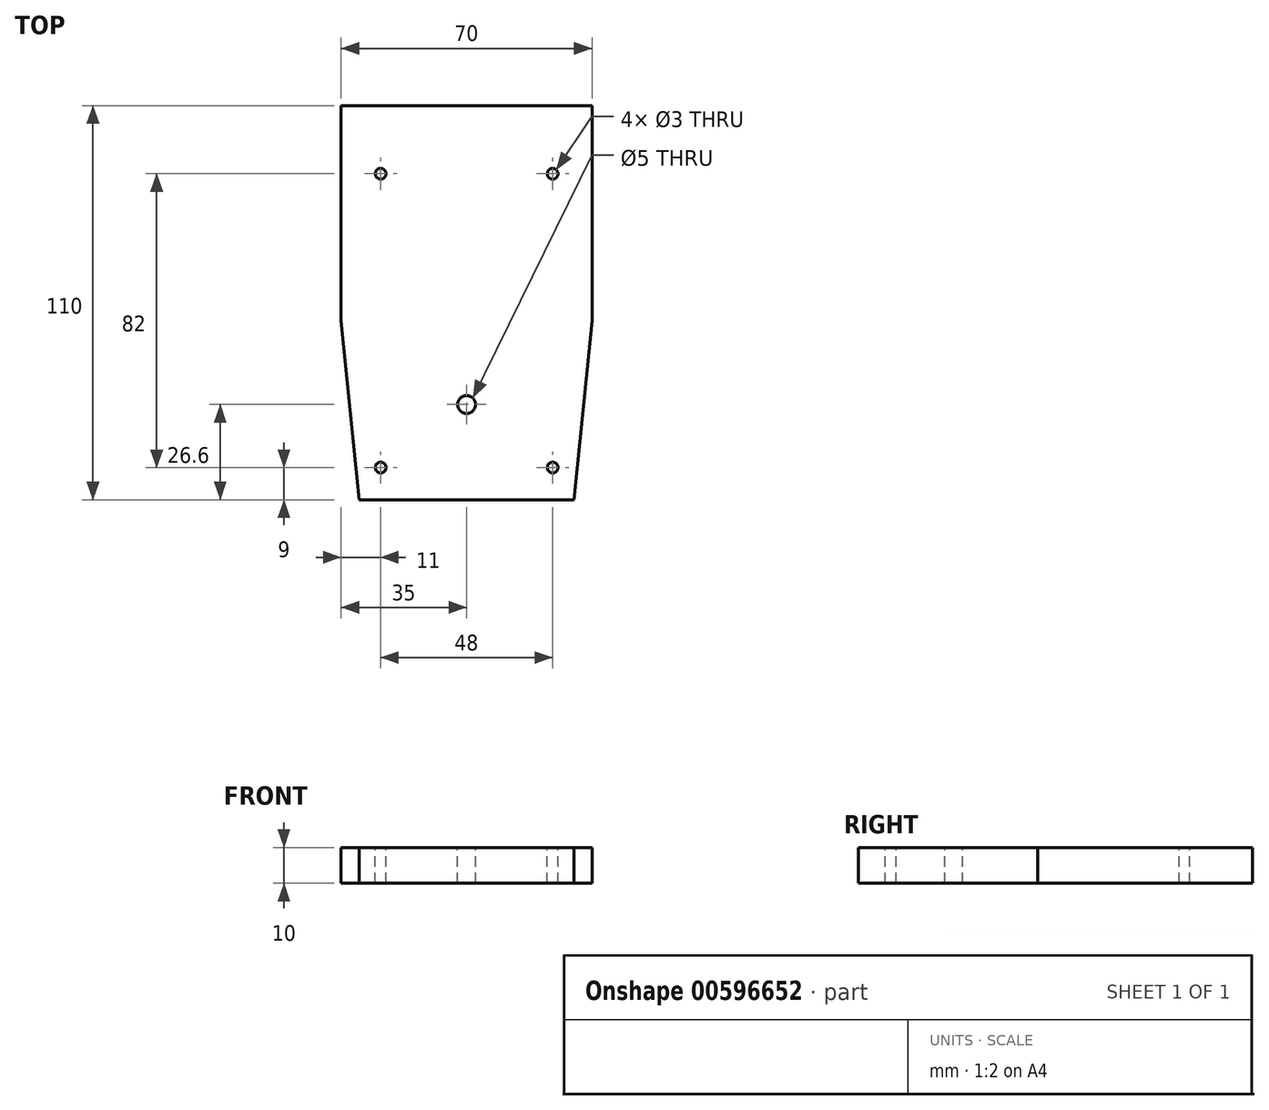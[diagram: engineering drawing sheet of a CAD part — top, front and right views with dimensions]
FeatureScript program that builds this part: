
annotation { "Feature Type Name" : "Feature", "Feature Type Description" : "" }
export const myFeature = defineFeature(function(context is Context, id is Id, definition is map)
    precondition{}
    {
        {
            var Q0;
            Q0=qCreatedBy(makeId("Top.planeOp"),FACE);
            var sketch = newSketch(context, id + "F0", { "sketchPlane" : qUnion([Q0])});
            skLineSegment(sketch, "E0.bottom", {"start": v(35, 55) * mm, "end": v(-35, 55) * mm});
            skLineSegment(sketch, "E0.top", {"start": v(30, -55) * mm, "end": v(-30, -55) * mm});
            skLineSegment(sketch, "E0.left", {"start": v(35, 55) * mm, "end": v(35, -5) * mm});
            skLineSegment(sketch, "E0.right", {"start": v(-35, 55) * mm, "end": v(-35, -5) * mm});
            skPoint(sketch, "E0.middle", {"position": v(0, 0) * mm});
            skLineSegment(sketch, "E1", {"start": v(-70.7, -5) * mm, "end": v(55.02, -5) * mm, "construction": true});
            skLineSegment(sketch, "E2", {"start": v(30, -57.27) * mm, "end": v(30, 7.3) * mm, "construction": true});
            skLineSegment(sketch, "E3", {"start": v(-30, -57.9) * mm, "end": v(-30, 7.93) * mm, "construction": true});
            skLineSegment(sketch, "E4", {"start": v(0, -71) * mm, "end": v(0, 65.02) * mm, "construction": true});
            skPoint(sketch, "E4.endSnap0", {"position": v(0, 55) * mm});
            skLineSegment(sketch, "E5", {"start": v(-30, -55) * mm, "end": v(-35, -5) * mm});
            skLineSegment(sketch, "E6", {"start": v(35, -5) * mm, "end": v(30, -55) * mm});
            skPoint(sketch, "E7.orphan", {"position": v(-35, -55) * mm});
            skPoint(sketch, "E8.orphan", {"position": v(35, -55) * mm});
            skSolve(sketch);
        }
        {
            var Q0;
            Q0=makeQuery(id+"F0.imprint","IMPRINT",FACE,{"disambiguationData":[TD([[makeQuery(id+"F0.imprint","IMPRINT",EDGE,{"derivedFrom":sQuery(id+"F0.wireOp",EDGE,"E0.bottom")}),1.0]])]});
            extrude(context, id + "F1", {"entities" : qUnion([Q0]), "depth" : 10 * mm, "offsetDistance" : 25 * mm});
        }
        {
            var Q0;
            Q0=makeQuery(id+"F1.opExtrude","CAP_FACE",FACE,{"disambiguationData":[OSD([sQuery(id+"F0.wireOp",EDGE,"E0.bottom"),sQuery(id+"F0.wireOp",EDGE,"E0.top"),sQuery(id+"F0.wireOp",EDGE,"E0.left"),sQuery(id+"F0.wireOp",EDGE,"E0.right"),sQuery(id+"F0.wireOp",EDGE,"E5"),sQuery(id+"F0.wireOp",EDGE,"E6")])],"isStart":false});
            var sketch = newSketch(context, id + "F2", { "sketchPlane" : qUnion([Q0])});
            skLineSegment(sketch, "E9", {"start": v(-80.97, 36) * mm, "end": v(80.97, 36) * mm, "construction": true});
            skLineSegment(sketch, "E10", {"start": v(-24, 60.66) * mm, "end": v(-24, -66.93) * mm, "construction": true});
            skLineSegment(sketch, "E11", {"start": v(24, 62.09) * mm, "end": v(24, -66.65) * mm, "construction": true});
            skPoint(sketch, "E12", {"position": v(24, 36) * mm});
            skPoint(sketch, "E13", {"position": v(-24, 36) * mm});
            skLineSegment(sketch, "E14", {"start": v(-79.03, -46) * mm, "end": v(83.88, -46) * mm, "construction": true});
            skPoint(sketch, "E15", {"position": v(-24, -46) * mm});
            skPoint(sketch, "E16", {"position": v(24, -46) * mm});
            skLineSegment(sketch, "E17", {"start": v(0, -61.23) * mm, "end": v(0, 63.51) * mm, "construction": true});
            skPoint(sketch, "E17.endSnap0", {"position": v(0, 55) * mm});
            skLineSegment(sketch, "E18", {"start": v(-54.9, -28.4) * mm, "end": v(59.3, -28.4) * mm, "construction": true});
            skLineSegment(sketch, "E19", {"start": v(69.27, 55) * mm, "end": v(-59.18, 55) * mm, "construction": true});
            skPoint(sketch, "E20", {"position": v(0, -28.4) * mm});
            skSolve(sketch);
        }
        {
            var Q0;
            Q0=sQuery(id+"F2.wireOp",VERTEX,"E20");
            var Q1;
            Q1=makeQuery(id+"F1.opExtrude","SWEPT_BODY",BODY,{"disambiguationData":[OSD([sQuery(id+"F0.wireOp",EDGE,"E0.bottom"),sQuery(id+"F0.wireOp",EDGE,"E0.top"),sQuery(id+"F0.wireOp",EDGE,"E0.left"),sQuery(id+"F0.wireOp",EDGE,"E0.right"),sQuery(id+"F0.wireOp",EDGE,"E5"),sQuery(id+"F0.wireOp",EDGE,"E6")])]});
            hole(context, id + "F3", {"style" : HoleStyle.SIMPLE, "endStyle" : HoleEndStyle.THROUGH, "holeDiameter" : 5 * mm, "majorDiameter" : 5 * mm, "isTappedThrough" : true, "tappedDepth" : 12 * mm, "tapClearance" : 3, "locations" : qUnion([Q0]), "scope" : qUnion([Q1])});
        }
        {
            var Q0;
            Q0=sQuery(id+"F2.wireOp",VERTEX,"E13");
            var Q1;
            Q1=sQuery(id+"F2.wireOp",VERTEX,"E12");
            var Q2;
            Q2=sQuery(id+"F2.wireOp",VERTEX,"E16");
            var Q3;
            Q3=sQuery(id+"F2.wireOp",VERTEX,"E15");
            var Q4;
            Q4=makeQuery(id+"F1.opExtrude","SWEPT_BODY",BODY,{"disambiguationData":[OSD([sQuery(id+"F0.wireOp",EDGE,"E0.bottom"),sQuery(id+"F0.wireOp",EDGE,"E0.top"),sQuery(id+"F0.wireOp",EDGE,"E0.left"),sQuery(id+"F0.wireOp",EDGE,"E0.right"),sQuery(id+"F0.wireOp",EDGE,"E5"),sQuery(id+"F0.wireOp",EDGE,"E6")])]});
            hole(context, id + "F4", {"style" : HoleStyle.SIMPLE, "endStyle" : HoleEndStyle.THROUGH, "holeDiameter" : 3 * mm, "majorDiameter" : 5 * mm, "isTappedThrough" : true, "tappedDepth" : 12 * mm, "tapClearance" : 3, "locations" : qUnion([Q0, Q1, Q2, Q3]), "scope" : qUnion([Q4])});
        }
    });
